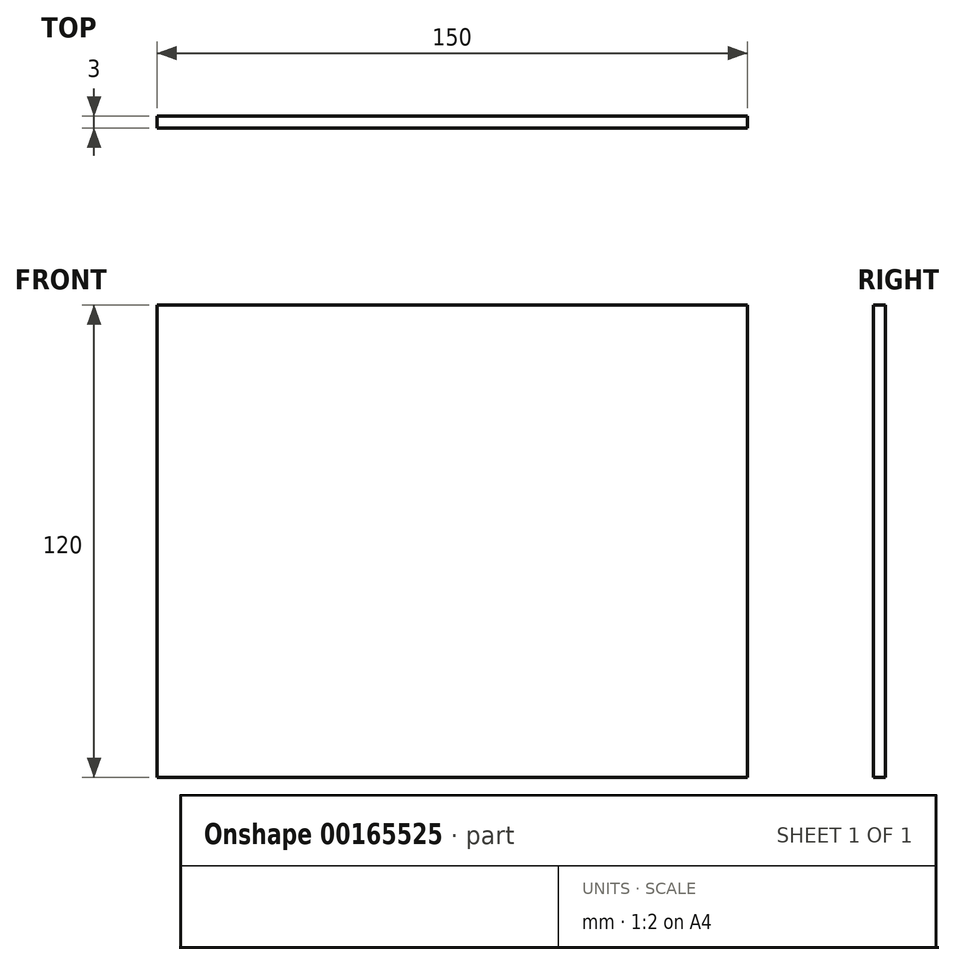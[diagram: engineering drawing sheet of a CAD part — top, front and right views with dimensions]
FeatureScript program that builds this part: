
annotation { "Feature Type Name" : "Feature", "Feature Type Description" : "" }
export const myFeature = defineFeature(function(context is Context, id is Id, definition is map)
    precondition{}
    {
        {
            var Q0;
            Q0=qCreatedBy(makeId("Front.planeOp"),FACE);
            var sketch = newSketch(context, id + "F0", { "sketchPlane" : qUnion([Q0])});
            skLineSegment(sketch, "E0.bottom", {"start": v(-62.77, 82.14) * mm, "end": v(87.23, 82.14) * mm});
            skLineSegment(sketch, "E0.top", {"start": v(-62.77, -37.86) * mm, "end": v(87.23, -37.86) * mm});
            skLineSegment(sketch, "E0.left", {"start": v(-62.77, 82.14) * mm, "end": v(-62.77, -37.86) * mm});
            skLineSegment(sketch, "E0.right", {"start": v(87.23, 82.14) * mm, "end": v(87.23, -37.86) * mm});
            skSolve(sketch);
        }
        {
            var Q0;
            Q0 = qSketchRegion(id + "F0", true);
            extrude(context, id + "F1", {"entities" : qUnion([Q0]), "depth" : 3 * mm});
        }
    });
